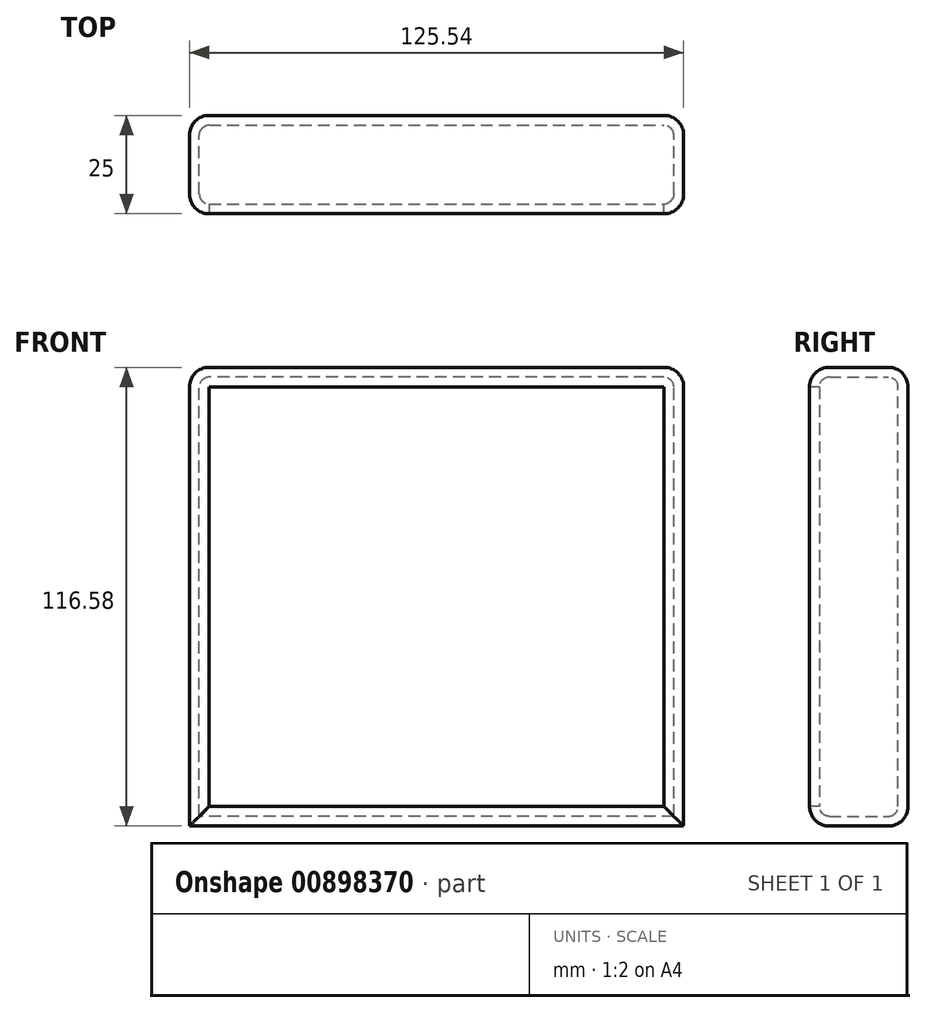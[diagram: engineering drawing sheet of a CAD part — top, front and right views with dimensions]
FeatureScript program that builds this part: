
annotation { "Feature Type Name" : "Feature", "Feature Type Description" : "" }
export const myFeature = defineFeature(function(context is Context, id is Id, definition is map)
    precondition{}
    {
        {
            var Q0;
            Q0=qCreatedBy(makeId("Front.planeOp"),FACE);
            var sketch = newSketch(context, id + "F0", { "sketchPlane" : qUnion([Q0])});
            skLineSegment(sketch, "E0.bottom", {"start": v(62.77, -58.3) * mm, "end": v(-62.77, -58.3) * mm});
            skLineSegment(sketch, "E0.top", {"start": v(62.77, 58.3) * mm, "end": v(-62.77, 58.3) * mm});
            skLineSegment(sketch, "E0.left", {"start": v(62.77, -58.3) * mm, "end": v(62.77, 58.3) * mm});
            skLineSegment(sketch, "E0.right", {"start": v(-62.77, -58.3) * mm, "end": v(-62.77, 58.3) * mm});
            skPoint(sketch, "E0.middle", {"position": v(0, 0) * mm});
            skSolve(sketch);
        }
        {
            var Q0;
            Q0 = qSketchRegion(id + "F0", true);
            extrude(context, id + "F1", {"entities" : qUnion([Q0]), "endBound" : BoundingType.SYMMETRIC, "depth" : 25 * mm, "offsetDistance" : 25 * mm});
        }
        {
            var Q0;
            Q0=makeQuery(id+"F1.opExtrude","SWEPT_FACE",FACE,{"disambiguationData":[OSD([sQuery(id+"F0.wireOp",EDGE,"E0.top")])]});
            var Q1;
            Q1=makeQuery(id+"F1.opExtrude","CAP_EDGE",EDGE,{"disambiguationData":[OSD([sQuery(id+"F0.wireOp",EDGE,"E0.left")])],"isStart":true});
            var Q2;
            Q2=makeQuery(id+"F1.opExtrude","CAP_FACE",FACE,{"disambiguationData":[OSD([sQuery(id+"F0.wireOp",EDGE,"E0.bottom"),sQuery(id+"F0.wireOp",EDGE,"E0.top"),sQuery(id+"F0.wireOp",EDGE,"E0.left"),sQuery(id+"F0.wireOp",EDGE,"E0.right")])],"isStart":false});
            var Q3;
            Q3=makeQuery(id+"F1.opExtrude","CAP_EDGE",EDGE,{"disambiguationData":[OSD([sQuery(id+"F0.wireOp",EDGE,"E0.right")])],"isStart":true});
            var Q4;
            Q4=makeQuery(id+"F1.opExtrude","CAP_FACE",FACE,{"disambiguationData":[OSD([sQuery(id+"F0.wireOp",EDGE,"E0.bottom"),sQuery(id+"F0.wireOp",EDGE,"E0.top"),sQuery(id+"F0.wireOp",EDGE,"E0.left"),sQuery(id+"F0.wireOp",EDGE,"E0.right")])],"isStart":true});
            var Q5;
            Q5=makeQuery(id+"F1.opExtrude","CAP_EDGE",EDGE,{"disambiguationData":[OSD([sQuery(id+"F0.wireOp",EDGE,"E0.bottom")])],"isStart":true});
            fillet(context, id + "F2", {"entities" : qUnion([Q0, Q1, Q2, Q3, Q4, Q5]), "radius" : 5 * mm, "tangentPropagation" : true, "allowEdgeOverflow" : false});
        }
        {
            var Q0;
            Q0=makeQuery(id+"F1.opExtrude","CAP_FACE",FACE,{"disambiguationData":[OSD([sQuery(id+"F0.wireOp",EDGE,"E0.bottom"),sQuery(id+"F0.wireOp",EDGE,"E0.top"),sQuery(id+"F0.wireOp",EDGE,"E0.left"),sQuery(id+"F0.wireOp",EDGE,"E0.right")])],"isStart":false});
            shell(context, id + "F3", {"entities" : qUnion([Q0]), "thickness" : 2.5 * mm});
        }
    });
